# Revit family: Vertikalbogen 90°- RBV 605 F FS.pdf jó
name_source: partatom
category: Generic Models
revit_build: Autodesk Revit 2017 (Build: 20190508_0315(x64)
units: mm (PartAtom-declared; Revit-internal decimal feet)

## family parameters
Always vertical = Yes
Can host rebar = No
Cut with Voids When Loaded = No
Part Type = Normal
Room Calculation Point = No
Round Connector Dimension = Use Diameter
Shared = No
Work Plane-Based = No

## types (8) — shared parameters
Cut's number = 2
Cut's number 2 = 4
Manufacturer = OBO BETTERMANN
Material = Strip galvanised
URL = http://www.obo-bettermann.com

## per-type parameters (varying)
| type | GTIN | Manufacturer Art.No. | Width |
| RBV 605 F FS | 4012195047438 | 7007051 | 50 mm  [stored 0.164042 ft] |
| RBV 610 F FS | 4012195047445 | 7007055 | 100 mm  [stored 0.328084 ft] |
| RBV 615 F FS | 4012195047452 | 7007059 | 150 mm |
| RBV 620 F FS | 4012195047469 | 7007063 | 200 mm  [stored 0.656168 ft] |
| RBV 630 F FS | 4012195047490 | 7007067 | 300 mm |
| RBV 640 F FS | 4012195047506 | 7007071 | 400 mm  [stored 1.31234 ft] |
| RBV 650 F FS | 4012195047513 | 7007075 | 500 mm  [stored 1.64042 ft] |
| RBV 660 F FS | 4012195047520 | 7007079 | 600 mm |

note: column(s) folded — value = type name in every type: Article Type

note: [stored X ft] marks values corroborated as IEEE doubles in the binary element streams (Revit-internal decimal feet)

## geometry (parser evidence)
native form markers: Sweep x2
no freeform markers — native parametric forms only
